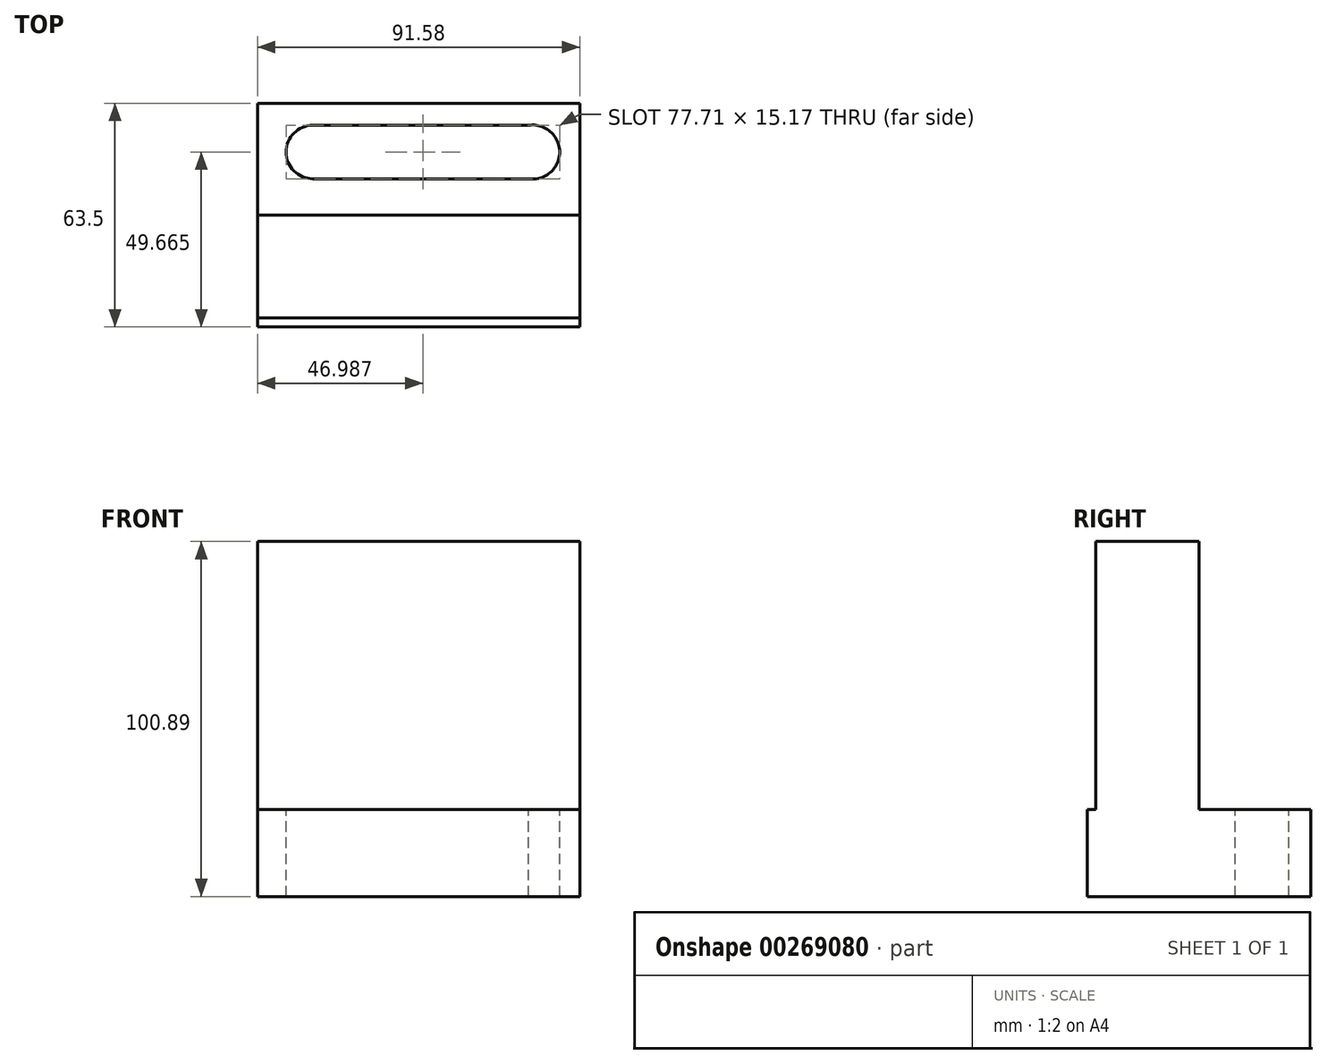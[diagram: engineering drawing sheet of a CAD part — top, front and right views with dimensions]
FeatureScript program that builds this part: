
annotation { "Feature Type Name" : "Feature", "Feature Type Description" : "" }
export const myFeature = defineFeature(function(context is Context, id is Id, definition is map)
    precondition{}
    {
        {
            var Q0;
            Q0=qCreatedBy(makeId("Front.planeOp"),FACE);
            var sketch = newSketch(context, id + "F0", { "sketchPlane" : qUnion([Q0])});
            skLineSegment(sketch, "E0.bottom", {"start": v(50.94, 39.18) * mm, "end": v(-40.64, 39.18) * mm});
            skLineSegment(sketch, "E0.top", {"start": v(50.94, 14.49) * mm, "end": v(-40.64, 14.49) * mm});
            skLineSegment(sketch, "E0.left", {"start": v(50.94, 39.18) * mm, "end": v(50.94, 14.49) * mm});
            skLineSegment(sketch, "E0.right", {"start": v(-40.64, 39.18) * mm, "end": v(-40.64, 14.49) * mm});
            skSolve(sketch);
        }
        {
            var Q0;
            Q0 = qSketchRegion(id + "F0", true);
            extrude(context, id + "F1", {"entities" : qUnion([Q0]), "depth" : 63.5 * mm});
        }
        {
            var Q0;
            Q0=makeQuery(id+"F1.opExtrude","SWEPT_FACE",FACE,{"disambiguationData":[OSD([sQuery(id+"F0.wireOp",EDGE,"E0.bottom")])]});
            var sketch = newSketch(context, id + "F2", { "sketchPlane" : qUnion([Q0])});
            skLineSegment(sketch, "E1.bottom", {"start": v(-24.92, -6.25) * mm, "end": v(37.53, -6.25) * mm});
            skLineSegment(sketch, "E1.top", {"start": v(-24.92, -21.42) * mm, "end": v(37.53, -21.42) * mm});
            skLineSegment(sketch, "E1.left", {"start": v(-24.92, -6.25) * mm, "end": v(-24.92, -21.42) * mm});
            skLineSegment(sketch, "E1.right", {"start": v(37.53, -6.25) * mm, "end": v(37.53, -21.42) * mm});
            skCircle(sketch, "E2", {"center": v(-24.92, -13.83) * mm, "radius": 7.58 * mm});
            skCircle(sketch, "E3", {"center": v(37.53, -13.83) * mm, "radius": 7.67 * mm});
            skSolve(sketch);
        }
        {
            var Q0;
            Q0 = qSketchRegion(id + "F2", true);
            extrude(context, id + "F3", {"entities" : qUnion([Q0]), "operationType" : NewBodyOperationType.REMOVE, "endBound" : BoundingType.THROUGH_ALL, "oppositeDirection" : true, "depth" : 25.4 * mm});
        }
        {
            var Q0;
            Q0=makeQuery(id+"F1.opExtrude","SWEPT_FACE",FACE,{"disambiguationData":[OSD([sQuery(id+"F0.wireOp",EDGE,"E0.bottom")])]});
            var sketch = newSketch(context, id + "F4", { "sketchPlane" : qUnion([Q0])});
            skLineSegment(sketch, "E4.bottom", {"start": v(-40.64, -61.03) * mm, "end": v(50.94, -61.03) * mm});
            skLineSegment(sketch, "E4.top", {"start": v(-40.64, -31.75) * mm, "end": v(50.94, -31.75) * mm});
            skLineSegment(sketch, "E4.left", {"start": v(-40.64, -61.03) * mm, "end": v(-40.64, -31.75) * mm});
            skLineSegment(sketch, "E4.right", {"start": v(50.94, -61.03) * mm, "end": v(50.94, -31.75) * mm});
            skSolve(sketch);
        }
        {
            var Q0;
            Q0 = qSketchRegion(id + "F4", true);
            extrude(context, id + "F5", {"entities" : qUnion([Q0]), "operationType" : NewBodyOperationType.ADD, "depth" : 76.2 * mm});
        }
    });
